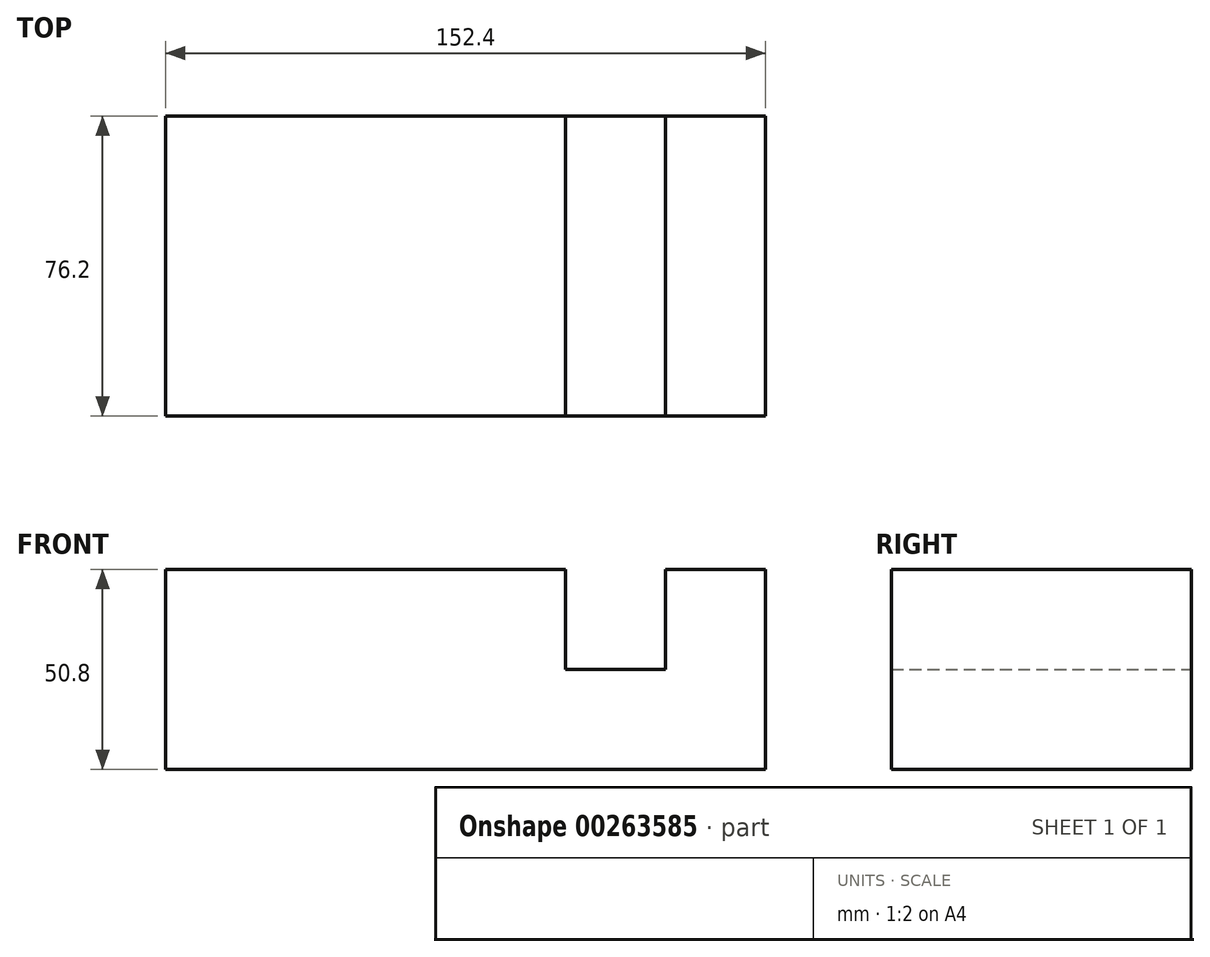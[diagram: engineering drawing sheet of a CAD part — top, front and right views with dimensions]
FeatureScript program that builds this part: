
annotation { "Feature Type Name" : "Feature", "Feature Type Description" : "" }
export const myFeature = defineFeature(function(context is Context, id is Id, definition is map)
    precondition{}
    {
        {
            var Q0;
            Q0=qCreatedBy(makeId("Front.planeOp"),FACE);
            var sketch = newSketch(context, id + "F0", { "sketchPlane" : qUnion([Q0])});
            skLineSegment(sketch, "E0.bottom", {"start": v(0, 0) * mm, "end": v(101.6, 0) * mm});
            skLineSegment(sketch, "E0.top", {"start": v(0, 50.8) * mm, "end": v(101.6, 50.8) * mm});
            skLineSegment(sketch, "E0.left", {"start": v(0, 0) * mm, "end": v(0, 50.8) * mm});
            skLineSegment(sketch, "E0.right", {"start": v(101.6, 0) * mm, "end": v(101.6, 50.8) * mm});
            skLineSegment(sketch, "E1.bottom", {"start": v(101.6, 0) * mm, "end": v(127, 0) * mm});
            skLineSegment(sketch, "E1.top", {"start": v(101.6, 25.4) * mm, "end": v(127, 25.4) * mm});
            skLineSegment(sketch, "E1.left", {"start": v(101.6, 0) * mm, "end": v(101.6, 25.4) * mm});
            skLineSegment(sketch, "E1.right", {"start": v(127, 0) * mm, "end": v(127, 25.4) * mm});
            skLineSegment(sketch, "E2.bottom", {"start": v(127, 0) * mm, "end": v(152.4, 0) * mm});
            skLineSegment(sketch, "E2.top", {"start": v(127, 50.8) * mm, "end": v(152.4, 50.8) * mm});
            skLineSegment(sketch, "E2.left", {"start": v(127, 0) * mm, "end": v(127, 50.8) * mm});
            skLineSegment(sketch, "E2.right", {"start": v(152.4, 0) * mm, "end": v(152.4, 50.8) * mm});
            skSolve(sketch);
        }
        {
            var Q0;
            Q0 = qSketchRegion(id + "F0", true);
            extrude(context, id + "F1", {"entities" : qUnion([Q0]), "depth" : 76.2 * mm});
        }
    });
